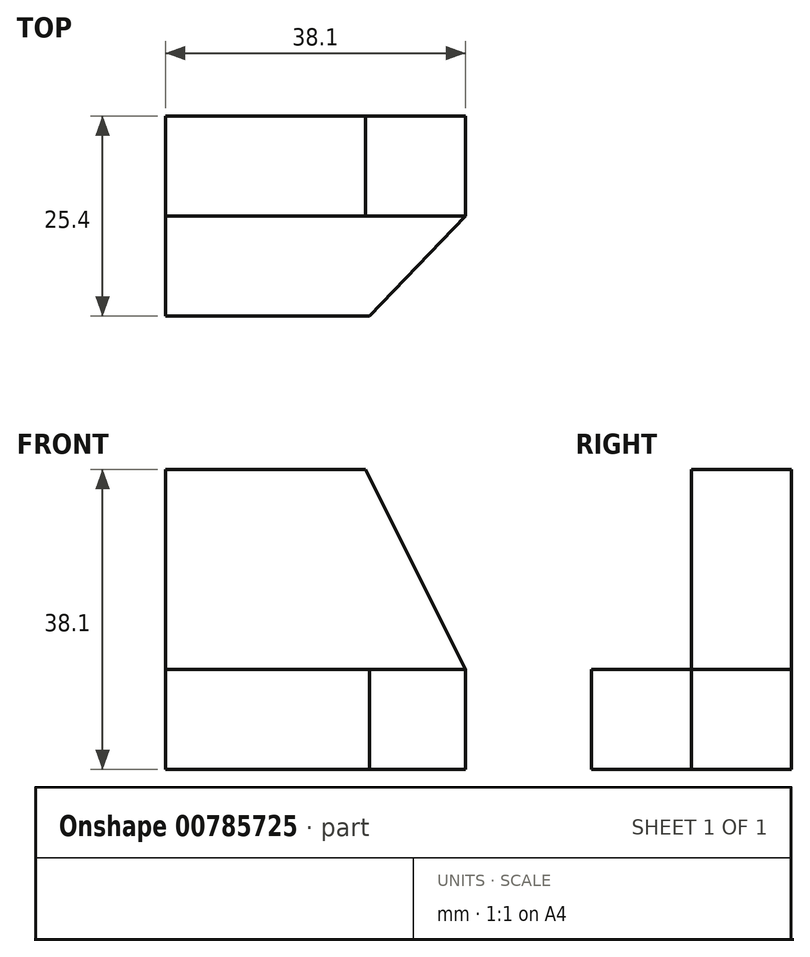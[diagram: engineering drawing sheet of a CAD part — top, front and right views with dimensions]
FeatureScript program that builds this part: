
annotation { "Feature Type Name" : "Feature", "Feature Type Description" : "" }
export const myFeature = defineFeature(function(context is Context, id is Id, definition is map)
    precondition{}
    {
        {
            var Q0;
            Q0=qCreatedBy(makeId("Front.planeOp"),FACE);
            var sketch = newSketch(context, id + "F0", { "sketchPlane" : qUnion([Q0])});
            skLineSegment(sketch, "E0", {"start": v(0, 0) * mm, "end": v(38.1, 0) * mm});
            skLineSegment(sketch, "E1", {"start": v(38.1, 0) * mm, "end": v(38.1, 38.1) * mm});
            skLineSegment(sketch, "E2", {"start": v(38.1, 38.1) * mm, "end": v(0, 38.1) * mm});
            skLineSegment(sketch, "E3", {"start": v(0, 38.1) * mm, "end": v(0, 0) * mm});
            skSolve(sketch);
        }
        {
            var Q0;
            Q0=makeQuery(id+"F0.imprint","IMPRINT",FACE,{"disambiguationData":[TD([[makeQuery(id+"F0.imprint","IMPRINT",EDGE,{"derivedFrom":sQuery(id+"F0.wireOp",EDGE,"E0")}),1.0]])]});
            var sketch = newSketch(context, id + "F1", { "sketchPlane" : qUnion([Q0])});
            skLineSegment(sketch, "E4", {"start": v(25.62, 38.08) * mm, "end": v(38.24, 12.83) * mm});
            skSolve(sketch);
        }
        {
            var Q0;
            Q0=makeQuery(id+"F1.imprint","IMPRINT",FACE,{"disambiguationData":[TD([[makeQuery(id+"F1.imprint","IMPRINT",EDGE,{"derivedFrom":makeQuery(id+"F0.imprint","IMPRINT",EDGE,{"derivedFrom":sQuery(id+"F0.wireOp",EDGE,"E0")})}),1.0]])]});
            extrude(context, id + "F2", {"entities" : qUnion([Q0]), "depth" : 25.4 * mm, "offsetDistance" : 25.4 * mm});
        }
        {
            var Q0;
            Q0=makeQuery(id+"F2.opExtrude","CAP_FACE",FACE,{"disambiguationData":[OSD([sQuery(id+"F0.wireOp",EDGE,"E0"),sQuery(id+"F0.wireOp",EDGE,"E1"),sQuery(id+"F0.wireOp",EDGE,"E2"),sQuery(id+"F0.wireOp",EDGE,"E3")])],"isStart":false});
            var sketch = newSketch(context, id + "F3", { "sketchPlane" : qUnion([Q0])});
            skLineSegment(sketch, "E5", {"start": v(38.1, 0) * mm, "end": v(38.1, 12.7) * mm});
            skLineSegment(sketch, "E6", {"start": v(0, 38.1) * mm, "end": v(25.4, 38.1) * mm});
            skLineSegment(sketch, "E7", {"start": v(25.4, 38.1) * mm, "end": v(38.1, 12.7) * mm});
            skSolve(sketch);
        }
        {
            var Q0;
            {var subQ0=sQuery(id+"F3.wireOp",EDGE,"E7");Q0=makeQuery(id+"F3.imprint","IMPRINT",FACE,{"disambiguationData":[TD([[makeQuery(id+"F3.imprint","IMPRINT",EDGE,{"derivedFrom":subQ0}),1.0]])]});}
            extrude(context, id + "F4", {"entities" : qUnion([Q0]), "operationType" : NewBodyOperationType.REMOVE, "oppositeDirection" : true, "depth" : 25.4 * mm, "offsetDistance" : 25.4 * mm});
        }
        {
            var Q0;
            Q0=makeQuery(id+"F2.opExtrude","SWEPT_FACE",FACE,{"disambiguationData":[OSD([sQuery(id+"F0.wireOp",EDGE,"E3")])]});
            var sketch = newSketch(context, id + "F5", { "sketchPlane" : qUnion([Q0])});
            skLineSegment(sketch, "E8", {"start": v(12.7, 38.1) * mm, "end": v(12.7, 12.7) * mm});
            skLineSegment(sketch, "E9", {"start": v(12.7, 12.7) * mm, "end": v(25.4, 12.7) * mm});
            skLineSegment(sketch, "E10", {"start": v(25.4, 12.7) * mm, "end": v(25.4, 38.1) * mm});
            skLineSegment(sketch, "E11", {"start": v(25.4, 38.1) * mm, "end": v(12.7, 38.1) * mm});
            skSolve(sketch);
        }
        {
            var Q0;
            Q0=makeQuery(id+"F5.imprint","IMPRINT",FACE,{"disambiguationData":[TD([[makeQuery(id+"F5.imprint","IMPRINT",EDGE,{"derivedFrom":sQuery(id+"F5.wireOp",EDGE,"E8")}),1.0]])]});
            extrude(context, id + "F6", {"entities" : qUnion([Q0]), "operationType" : NewBodyOperationType.REMOVE, "oppositeDirection" : true, "depth" : 38.1 * mm, "offsetDistance" : 25.4 * mm});
        }
        {
            var Q0;
            Q0=makeQuery(id+"F6.boolean.opBoolean","COPY",FACE,{"derivedFrom":makeQuery(id+"F6.opExtrude","SWEPT_FACE",FACE,{"disambiguationData":[OSD([sQuery(id+"F5.wireOp",EDGE,"E9")])]})});
            var sketch = newSketch(context, id + "F7", { "sketchPlane" : qUnion([Q0])});
            skLineSegment(sketch, "E12", {"start": v(38.1, -12.7) * mm, "end": v(25.9, -25.4) * mm});
            skSolve(sketch);
        }
        {
            var Q0;
            {var subQ0=sQuery(id+"F7.wireOp",EDGE,"E12");Q0=makeQuery(id+"F7.imprint","IMPRINT",FACE,{"disambiguationData":[TD([[makeQuery(id+"F7.imprint","IMPRINT",EDGE,{"derivedFrom":subQ0}),1.0]])]});}
            extrude(context, id + "F8", {"entities" : qUnion([Q0]), "operationType" : NewBodyOperationType.REMOVE, "oppositeDirection" : true, "depth" : 25.4 * mm, "offsetDistance" : 25.4 * mm});
        }
    });
